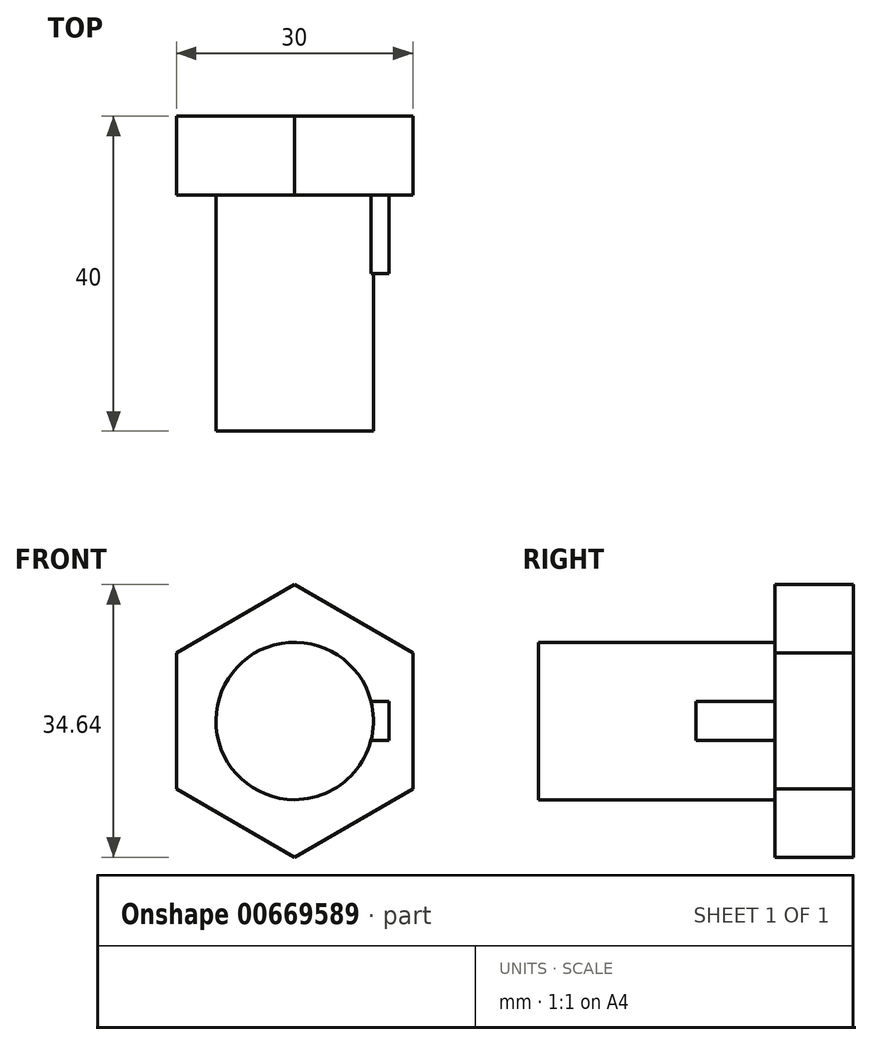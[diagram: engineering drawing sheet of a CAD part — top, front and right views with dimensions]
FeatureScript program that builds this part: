
annotation { "Feature Type Name" : "Feature", "Feature Type Description" : "" }
export const myFeature = defineFeature(function(context is Context, id is Id, definition is map)
    precondition{}
    {
        {
            var Q0;
            Q0=qCreatedBy(makeId("Front.planeOp"),FACE);
            var sketch = newSketch(context, id + "F0", { "sketchPlane" : qUnion([Q0])});
            skCircle(sketch, "E0.cCircle", {"center": v(0, 0) * mm, "radius": 15 * mm, "construction": true});
            skLineSegment(sketch, "E0.0", {"start": v(-14.96, 8.73) * mm, "end": v(0.08, 17.32) * mm});
            skLineSegment(sketch, "E0.1", {"start": v(0.08, 17.32) * mm, "end": v(15.04, 8.6) * mm});
            skLineSegment(sketch, "E0.2", {"start": v(15.04, 8.6) * mm, "end": v(14.96, -8.73) * mm});
            skLineSegment(sketch, "E0.3", {"start": v(14.96, -8.73) * mm, "end": v(-0.08, -17.32) * mm});
            skLineSegment(sketch, "E0.4", {"start": v(-0.08, -17.32) * mm, "end": v(-15.04, -8.6) * mm});
            skLineSegment(sketch, "E0.5", {"start": v(-15.04, -8.6) * mm, "end": v(-14.96, 8.73) * mm});
            skPoint(sketch, "E0.0.midPoint", {"position": v(-7.44, 13.02) * mm});
            skCircle(sketch, "E1", {"center": v(0, 0) * mm, "radius": 10 * mm});
            skLineSegment(sketch, "E2.bottom", {"start": v(12, -2.5) * mm, "end": v(9.68, -2.5) * mm});
            skLineSegment(sketch, "E2.top", {"start": v(12, 2.5) * mm, "end": v(9.68, 2.5) * mm});
            skLineSegment(sketch, "E2.left", {"start": v(12, -2.5) * mm, "end": v(12, 2.5) * mm});
            skPoint(sketch, "E2.middle", {"position": v(10, 0) * mm});
            skPoint(sketch, "E2.right.end.orphan", {"position": v(8, 2.5) * mm});
            skPoint(sketch, "E3.orphan", {"position": v(8, -2.5) * mm});
            skSolve(sketch);
        }
        {
            var Q0;
            {var subQ0=sQuery(id+"F0.wireOp",EDGE,"E1");var subQ1=makeQuery(id+"F0.imprint","INTERSECT",VERTEX,{"derivedFrom":[subQ0,sQuery(id+"F0.wireOp",EDGE,"E2.bottom")]});Q0=makeQuery(id+"F0.imprint","IMPRINT",FACE,{"disambiguationData":[TD([[makeQuery(id+"F0.imprint","IMPRINT",EDGE,{"disambiguationData":[TD([[subQ1,1.0]])],"derivedFrom":subQ0}),1.0]])]});}
            extrude(context, id + "F1", {"entities" : qUnion([Q0]), "depth" : 30 * mm, "offsetDistance" : 25 * mm});
        }
        {
            var Q0;
            {var subQ0=sQuery(id+"F0.wireOp",EDGE,"E2.bottom");Q0=makeQuery(id+"F0.imprint","IMPRINT",FACE,{"disambiguationData":[TD([[makeQuery(id+"F0.imprint","IMPRINT",EDGE,{"derivedFrom":subQ0}),-1.0]])]});}
            extrude(context, id + "F2", {"entities" : qUnion([Q0]), "operationType" : NewBodyOperationType.ADD, "depth" : 10 * mm, "offsetDistance" : 25 * mm});
        }
        {
            var Q0;
            Q0=qCreatedBy(makeId("Front.planeOp"),FACE);
            var sketch = newSketch(context, id + "F3", { "sketchPlane" : qUnion([Q0])});
            skCircle(sketch, "E4.cCircle", {"center": v(0, 0) * mm, "radius": 15 * mm, "construction": true});
            skLineSegment(sketch, "E4.0", {"start": v(-15, -8.66) * mm, "end": v(-15, 8.66) * mm});
            skLineSegment(sketch, "E4.1", {"start": v(-15, 8.66) * mm, "end": v(0, 17.32) * mm});
            skLineSegment(sketch, "E4.2", {"start": v(0, 17.32) * mm, "end": v(15, 8.66) * mm});
            skLineSegment(sketch, "E4.3", {"start": v(15, 8.66) * mm, "end": v(15, -8.66) * mm});
            skLineSegment(sketch, "E4.4", {"start": v(15, -8.66) * mm, "end": v(0, -17.32) * mm});
            skLineSegment(sketch, "E4.5", {"start": v(0, -17.32) * mm, "end": v(-15, -8.66) * mm});
            skPoint(sketch, "E4.0.midPoint", {"position": v(-15, 0) * mm});
            skSolve(sketch);
        }
        {
            var Q0;
            Q0=makeQuery(id+"F3.imprint","IMPRINT",FACE,{"disambiguationData":[TD([[makeQuery(id+"F3.imprint","IMPRINT",EDGE,{"derivedFrom":sQuery(id+"F3.wireOp",EDGE,"E4.0")}),-1.0]])]});
            extrude(context, id + "F4", {"entities" : qUnion([Q0]), "operationType" : NewBodyOperationType.ADD, "oppositeDirection" : true, "depth" : 10 * mm, "offsetDistance" : 25 * mm});
        }
    });
